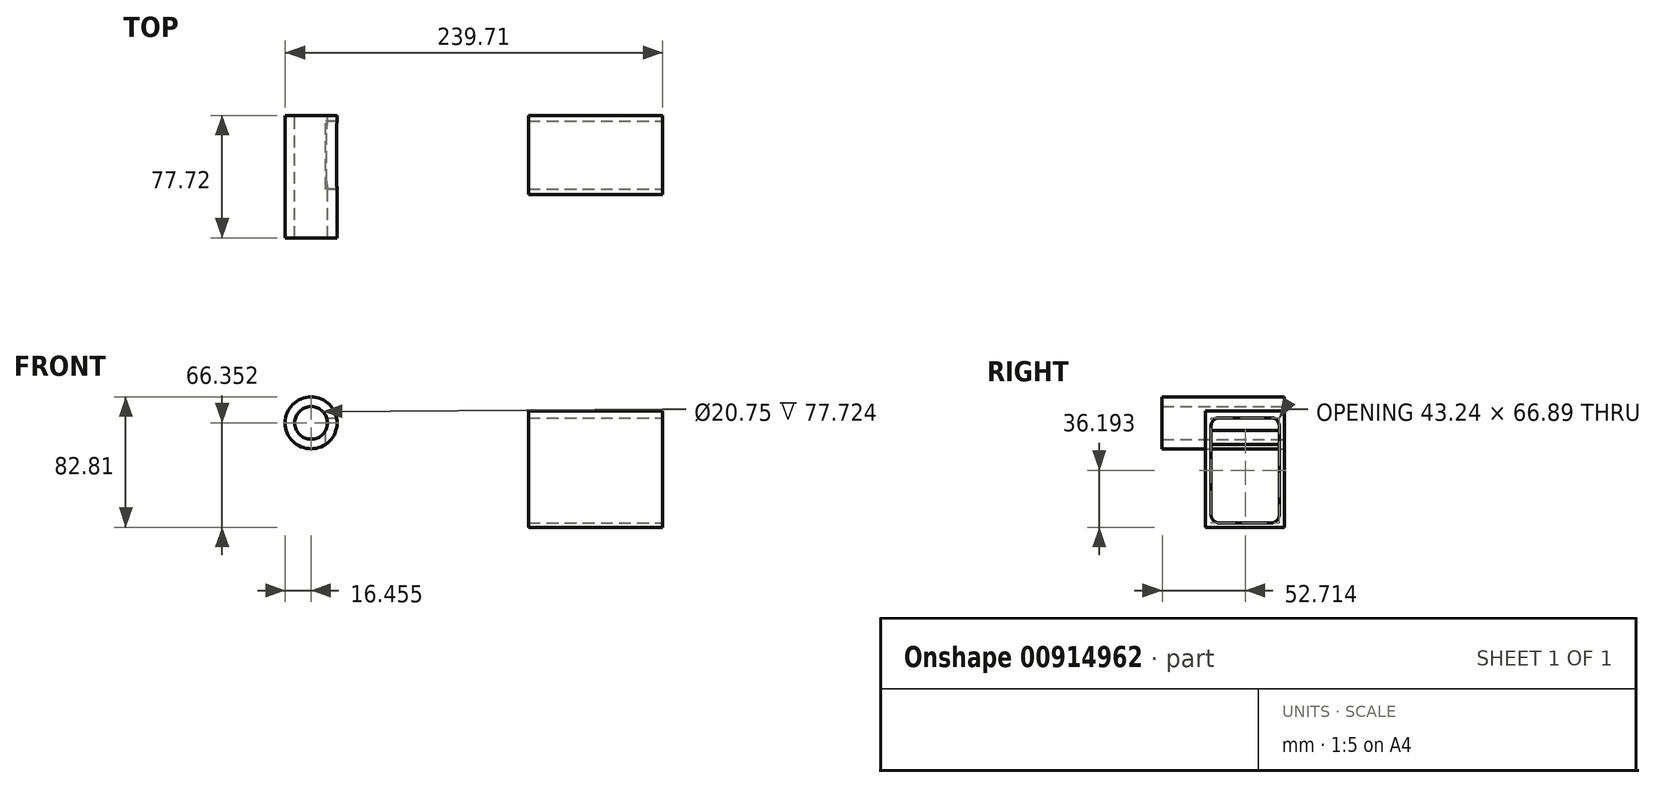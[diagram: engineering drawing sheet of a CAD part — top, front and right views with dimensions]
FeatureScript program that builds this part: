
annotation { "Feature Type Name" : "Feature", "Feature Type Description" : "" }
export const myFeature = defineFeature(function(context is Context, id is Id, definition is map)
    precondition{}
    {
        {
            var Q0;
            Q0=qCreatedBy(makeId("Front.planeOp"),FACE);
            var sketch = newSketch(context, id + "F0", { "sketchPlane" : qUnion([Q0])});
            skCircle(sketch, "E0", {"center": v(-66.55, 27.2) * mm, "radius": 16.46 * mm});
            skCircle(sketch, "E1", {"center": v(-66.55, 27.2) * mm, "radius": 10.38 * mm});
            skSolve(sketch);
        }
        {
            var Q0;
            Q0=makeQuery(id+"F0.imprint","IMPRINT",FACE,{"disambiguationData":[TD([[makeQuery(id+"F0.imprint","IMPRINT",EDGE,{"derivedFrom":sQuery(id+"F0.wireOp",EDGE,"E1")}),1.0]])]});
            var Q1;
            Q1=makeQuery(id+"F0.imprint","IMPRINT",FACE,{"disambiguationData":[TD([[makeQuery(id+"F0.imprint","IMPRINT",EDGE,{"derivedFrom":sQuery(id+"F0.wireOp",EDGE,"E0")}),1.0]])]});
            extrude(context, id + "F1", {"entities" : qUnion([Q0, Q1]), "depth" : 77.72 * mm, "offsetDistance" : 25.4 * mm});
        }
        {
            var Q0;
            Q0=makeQuery(id+"F1.opExtrude","CAP_FACE",FACE,{"disambiguationData":[OSD([sQuery(id+"F0.wireOp",EDGE,"E0")])],"isStart":true});
            var sketch = newSketch(context, id + "F2", { "sketchPlane" : qUnion([Q0])});
            skCircle(sketch, "E2", {"center": v(66.55, 27.2) * mm, "radius": 10.38 * mm});
            skSolve(sketch);
        }
        {
            var Q0;
            Q0=makeQuery(id+"F2.imprint","IMPRINT",FACE,{"disambiguationData":[TD([[makeQuery(id+"F2.imprint","IMPRINT",EDGE,{"derivedFrom":sQuery(id+"F2.wireOp",EDGE,"E2")}),1.0]])]});
            extrude(context, id + "F3", {"entities" : qUnion([Q0]), "operationType" : NewBodyOperationType.REMOVE, "oppositeDirection" : true, "depth" : 121.16 * mm, "offsetDistance" : 25.4 * mm});
        }
        {
            var Q0;
            Q0=qCreatedBy(makeId("Front.planeOp"),FACE);
            var sketch = newSketch(context, id + "F4", { "sketchPlane" : qUnion([Q0])});
            skLineSegment(sketch, "E3.bottom", {"start": v(71.49, 34.64) * mm, "end": v(156.7, 34.64) * mm});
            skLineSegment(sketch, "E3.top", {"start": v(71.49, -39.15) * mm, "end": v(156.7, -39.15) * mm});
            skLineSegment(sketch, "E3.left", {"start": v(71.49, 34.64) * mm, "end": v(71.49, -39.15) * mm});
            skLineSegment(sketch, "E3.right", {"start": v(156.7, 34.64) * mm, "end": v(156.7, -39.15) * mm});
            skSolve(sketch);
        }
        {
            var Q0;
            Q0 = qSketchRegion(id + "F4", true);
            extrude(context, id + "F5", {"entities" : qUnion([Q0]), "depth" : 50.3 * mm, "offsetDistance" : 25.4 * mm});
        }
        {
            var Q0;
            Q0=makeQuery(id+"F5.opExtrude","SWEPT_FACE",FACE,{"disambiguationData":[OSD([sQuery(id+"F4.wireOp",EDGE,"E3.right")])]});
            var sketch = newSketch(context, id + "F6", { "sketchPlane" : qUnion([Q0])});
            skLineSegment(sketch, "E4.bottom", {"start": v(-3.39, -36.4) * mm, "end": v(-46.62, -36.4) * mm});
            skLineSegment(sketch, "E4.top", {"start": v(-3.39, 30.49) * mm, "end": v(-46.62, 30.49) * mm});
            skLineSegment(sketch, "E4.left", {"start": v(-3.39, -36.4) * mm, "end": v(-3.39, 30.49) * mm});
            skLineSegment(sketch, "E4.right", {"start": v(-46.62, -36.4) * mm, "end": v(-46.62, 30.49) * mm});
            skSolve(sketch);
        }
        {
            var Q0;
            Q0 = qSketchRegion(id + "F6", true);
            extrude(context, id + "F7", {"entities" : qUnion([Q0]), "operationType" : NewBodyOperationType.REMOVE, "oppositeDirection" : true, "depth" : 214.12 * mm, "offsetDistance" : 25.4 * mm});
        }
        {
            var Q0;
            Q0=makeQuery(id+"F7.boolean.opBoolean","COPY",EDGE,{"derivedFrom":makeQuery(id+"F7.opExtrude","SWEPT_EDGE",EDGE,{"disambiguationData":[OSD([sQuery(id+"F6.wireOp",EDGE,"E4.top"),sQuery(id+"F6.wireOp",EDGE,"E4.left")])]})});
            var Q1;
            Q1=makeQuery(id+"F7.boolean.opBoolean","COPY",EDGE,{"derivedFrom":makeQuery(id+"F7.opExtrude","SWEPT_EDGE",EDGE,{"disambiguationData":[OSD([sQuery(id+"F6.wireOp",EDGE,"E4.top"),sQuery(id+"F6.wireOp",EDGE,"E4.right")])]})});
            var Q2;
            Q2=makeQuery(id+"F7.boolean.opBoolean","COPY",EDGE,{"derivedFrom":makeQuery(id+"F7.opExtrude","SWEPT_EDGE",EDGE,{"disambiguationData":[OSD([sQuery(id+"F6.wireOp",EDGE,"E4.bottom"),sQuery(id+"F6.wireOp",EDGE,"E4.right")])]})});
            var Q3;
            Q3=makeQuery(id+"F7.boolean.opBoolean","COPY",EDGE,{"derivedFrom":makeQuery(id+"F7.opExtrude","SWEPT_EDGE",EDGE,{"disambiguationData":[OSD([sQuery(id+"F6.wireOp",EDGE,"E4.bottom"),sQuery(id+"F6.wireOp",EDGE,"E4.left")])]})});
            fillet(context, id + "F8", {"entities" : qUnion([Q0, Q1, Q2, Q3]), "radius" : 5.08 * mm, "tangentPropagation" : true, "allowEdgeOverflow" : false});
        }
    });
